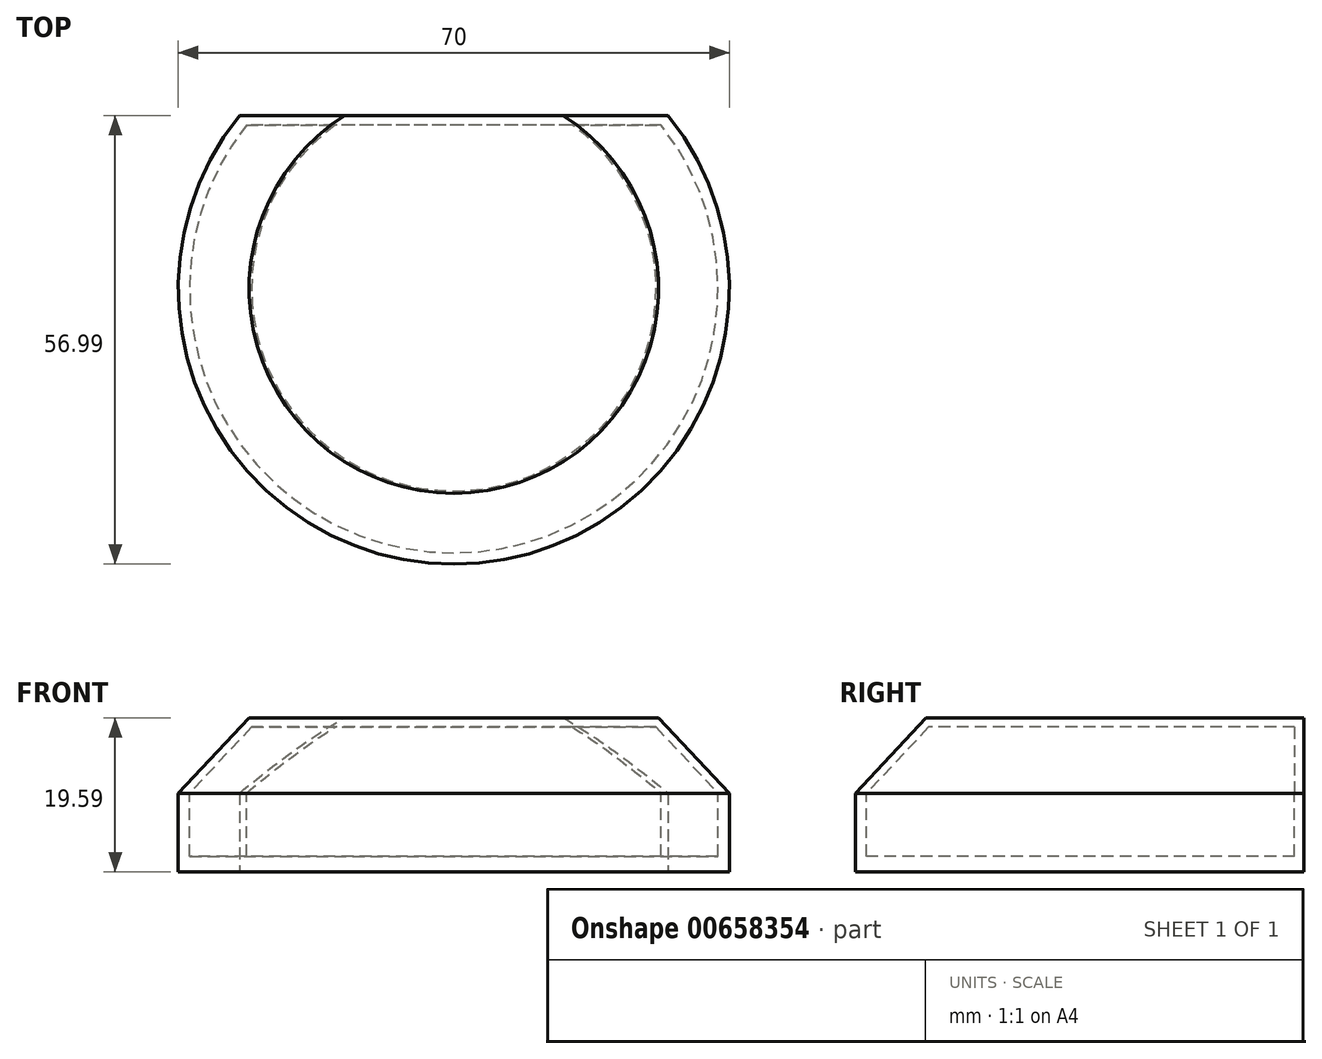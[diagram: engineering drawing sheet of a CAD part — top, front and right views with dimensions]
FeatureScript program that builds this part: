
annotation { "Feature Type Name" : "Feature", "Feature Type Description" : "" }
export const myFeature = defineFeature(function(context is Context, id is Id, definition is map)
    precondition{}
    {
        {
            var Q0;
            Q0=qCreatedBy(makeId("Top.planeOp"),FACE);
            var sketch = newSketch(context, id + "F0", { "sketchPlane" : qUnion([Q0])});
            skArc(sketch, "E0", {"start": v(-27.23, 21.99) * mm, "mid": v(0, -35) * mm, "end": v(27.23, 22) * mm});
            skLineSegment(sketch, "E1", {"start": v(-27.23, 22) * mm, "end": v(27.23, 22) * mm});
            skSolve(sketch);
        }
        {
            var Q0;
            Q0 = qSketchRegion(id + "F0", true);
            extrude(context, id + "F1", {"entities" : qUnion([Q0]), "depth" : 2 * mm, "offsetDistance" : 25 * mm});
        }
        {
            var Q0;
            Q0=qCreatedBy(makeId("Front.planeOp"),FACE);
            var sketch = newSketch(context, id + "F2", { "sketchPlane" : qUnion([Q0])});
            skLineSegment(sketch, "E2", {"start": v(0, 0) * mm, "end": v(-35, 0) * mm});
            skLineSegment(sketch, "E3", {"start": v(-35, 0) * mm, "end": v(-35, 10) * mm});
            skLineSegment(sketch, "E4", {"start": v(-35, 10) * mm, "end": v(-26, 19.59) * mm});
            skLineSegment(sketch, "E5", {"start": v(-26, 19.59) * mm, "end": v(0, 19.59) * mm});
            skLineSegment(sketch, "E6", {"start": v(0, 27.44) * mm, "end": v(0, -2.62) * mm, "construction": true});
            skLineSegment(sketch, "E7", {"start": v(-35, 0) * mm, "end": v(-33.56, 0) * mm});
            skLineSegment(sketch, "E8", {"start": v(-33.56, 0) * mm, "end": v(-33.56, 10) * mm});
            skLineSegment(sketch, "E9", {"start": v(0, 19.59) * mm, "end": v(0, 18.39) * mm});
            skLineSegment(sketch, "E10", {"start": v(0, 18.39) * mm, "end": v(-26, 18.39) * mm});
            skLineSegment(sketch, "E11", {"start": v(-33.56, 10) * mm, "end": v(-25.69, 18.39) * mm});
            skSolve(sketch);
        }
        {
            var Q0;
            Q0 = qSketchRegion(id + "F2", true);
            var Q1;
            Q1=sQuery(id+"F2.wireOp",EDGE,"E6");
            revolve(context, id + "F3", {"operationType" : NewBodyOperationType.ADD, "entities" : qUnion([Q0]), "axis" : qUnion([Q1]), "revolveType" : RevolveType.FULL});
        }
        {
            var Q0;
            Q0=makeQuery(id+"F3.boolean.opBoolean","MERGE",FACE,{"derivedFrom":[makeQuery(id+"F1.opExtrude","CAP_FACE",FACE,{"disambiguationData":[OSD([sQuery(id+"F0.wireOp",EDGE,"E0"),sQuery(id+"F0.wireOp",EDGE,"E1")])],"isStart":true}),makeQuery(id+"F3.opRevolve","SWEPT_FACE",FACE,{"disambiguationData":[OSD([sQuery(id+"F2.wireOp",EDGE,"E7")])]})]});
            var sketch = newSketch(context, id + "F4", { "sketchPlane" : qUnion([Q0])});
            skLineSegment(sketch, "E12", {"start": v(-25.35, -22) * mm, "end": v(27.23, -22) * mm});
            skLineSegment(sketch, "E13", {"start": v(27.23, -22) * mm, "end": v(-27.23, -22) * mm});
            skLineSegment(sketch, "E14", {"start": v(-27.23, -22) * mm, "end": v(-27.23, -37.24) * mm});
            skLineSegment(sketch, "E15", {"start": v(-27.23, -37.24) * mm, "end": v(27.23, -37.24) * mm});
            skLineSegment(sketch, "E16", {"start": v(27.23, -37.24) * mm, "end": v(27.23, -22) * mm});
            skSolve(sketch);
        }
        {
            var Q0;
            Q0 = qSketchRegion(id + "F4", true);
            extrude(context, id + "F5", {"entities" : qUnion([Q0]), "operationType" : NewBodyOperationType.REMOVE, "endBound" : BoundingType.THROUGH_ALL, "oppositeDirection" : true, "depth" : 25 * mm, "offsetDistance" : 25 * mm});
        }
        {
            var Q0;
            Q0=makeQuery(id+"F5.boolean.opBoolean","MERGE",FACE,{"derivedFrom":[makeQuery(id+"F1.opExtrude","SWEPT_FACE",FACE,{"disambiguationData":[OSD([sQuery(id+"F0.wireOp",EDGE,"E1")])]}),makeQuery(id+"F5.opExtrude","SWEPT_FACE",FACE,{"disambiguationData":[OSD([sQuery(id+"F4.wireOp",EDGE,"E13")])]})]});
            var sketch = newSketch(context, id + "F6", { "sketchPlane" : qUnion([Q0])});
            skLineSegment(sketch, "E17", {"start": v(-13.87, 19.59) * mm, "end": v(-27.23, 10) * mm});
            skLineSegment(sketch, "E18", {"start": v(-27.23, 10) * mm, "end": v(-27.23, 0) * mm});
            skLineSegment(sketch, "E19", {"start": v(-27.23, 0) * mm, "end": v(27.23, 0) * mm});
            skLineSegment(sketch, "E20", {"start": v(27.23, 0) * mm, "end": v(27.23, 10) * mm});
            skLineSegment(sketch, "E21", {"start": v(27.23, 10) * mm, "end": v(13.87, 19.59) * mm});
            skLineSegment(sketch, "E22", {"start": v(13.87, 19.59) * mm, "end": v(-13.87, 19.59) * mm});
            skSolve(sketch);
        }
        {
            var Q0;
            Q0 = qSketchRegion(id + "F6", true);
            extrude(context, id + "F7", {"entities" : qUnion([Q0]), "operationType" : NewBodyOperationType.ADD, "oppositeDirection" : true, "depth" : 1.2 * mm, "offsetDistance" : 25 * mm});
        }
    });
